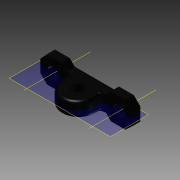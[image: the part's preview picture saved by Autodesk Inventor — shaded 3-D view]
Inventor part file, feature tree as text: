
AUTODESK INVENTOR PART (.ipt)
format: ipt  version: 2015 SP1 (Build 190203100, 203)  size: 373,248 bytes
history: native  units: in
note: dims shown in document units (in); Inventor stores cm internally (conversion verified against a paired STEP export)
features: other x4, plane x1, imported_body x1
ambient origin geometry x8: Origin, YZ Plane, XZ Plane, XY Plane, X Axis, Y Axis, Z Axis, Center Point
bodies: Body1 (feature_tree)
feature tree (6):
  other  "Pillow Block"
  parser-record x1  (decoder bookkeeping rows leaked as tree rows — omitted from the tree; the rows remain in map.json)
  plane  "Work Plane1"
  imported_body  "Base1"
  other  "Work Axis4"
  other  "Work Axis5"
